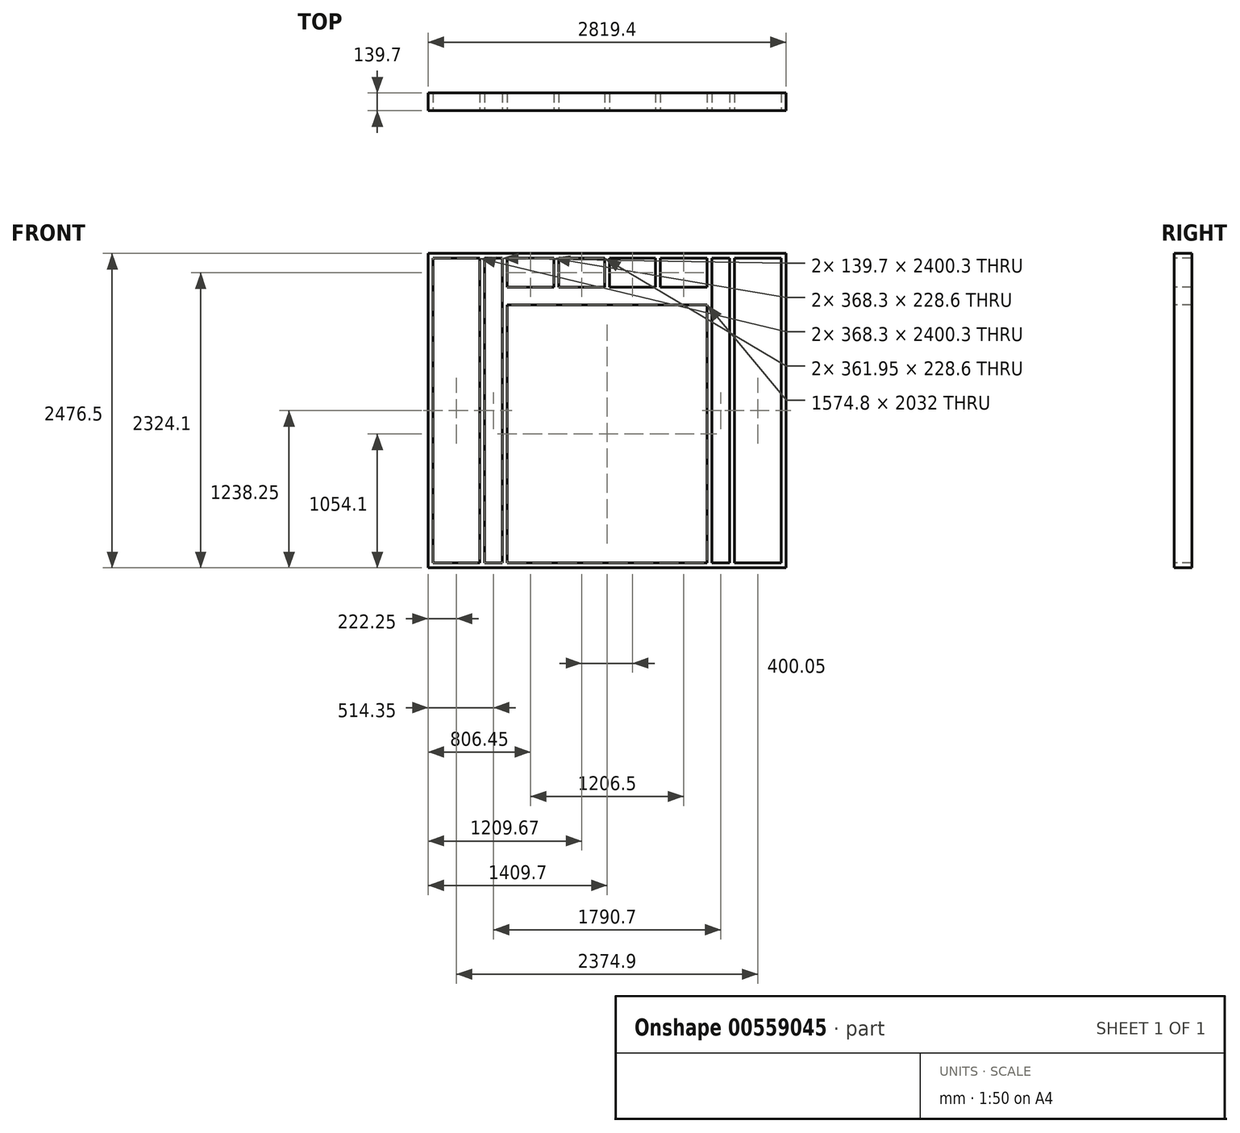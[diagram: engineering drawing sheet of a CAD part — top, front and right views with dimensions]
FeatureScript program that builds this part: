
annotation { "Feature Type Name" : "Feature", "Feature Type Description" : "" }
export const myFeature = defineFeature(function(context is Context, id is Id, definition is map)
    precondition{}
    {
        {
            var Q0;
            Q0=qCreatedBy(makeId("Front.planeOp"),FACE);
            var sketch = newSketch(context, id + "F0", { "sketchPlane" : qUnion([Q0])});
            skLineSegment(sketch, "E0.bottom", {"start": v(0, 0) * mm, "end": v(2819.4, 0) * mm});
            skLineSegment(sketch, "E0.top", {"start": v(0, 2476.5) * mm, "end": v(2819.4, 2476.5) * mm});
            skLineSegment(sketch, "E0.left", {"start": v(0, 0) * mm, "end": v(0, 2476.5) * mm});
            skLineSegment(sketch, "E0.right", {"start": v(2819.4, 0) * mm, "end": v(2819.4, 2476.5) * mm});
            skSolve(sketch);
        }
        {
            var Q0;
            Q0=qSketchRegion(id+"F0",true);
            extrude(context, id + "F1", {"entities" : qUnion([Q0]), "depth" : 139.7 * mm, "offsetDistance" : 25.4 * mm});
        }
        {
            var Q0;
            Q0=makeQuery(id+"F1.opExtrude","CAP_FACE",FACE,{"disambiguationData":[OSD([sQuery(id+"F0.wireOp",EDGE,"E0.bottom"),sQuery(id+"F0.wireOp",EDGE,"E0.top"),sQuery(id+"F0.wireOp",EDGE,"E0.left"),sQuery(id+"F0.wireOp",EDGE,"E0.right")])],"isStart":false});
            var sketch = newSketch(context, id + "F2", { "sketchPlane" : qUnion([Q0])});
            skLineSegment(sketch, "E1.bottom", {"start": v(622.3, 38.1) * mm, "end": v(2197.1, 38.1) * mm});
            skLineSegment(sketch, "E1.top", {"start": v(622.3, 2070.1) * mm, "end": v(2197.1, 2070.1) * mm});
            skLineSegment(sketch, "E1.left", {"start": v(622.3, 38.1) * mm, "end": v(622.3, 2070.1) * mm});
            skLineSegment(sketch, "E1.right", {"start": v(2197.1, 38.1) * mm, "end": v(2197.1, 2070.1) * mm});
            skLineSegment(sketch, "E2", {"start": v(622.3, 38.1) * mm, "end": v(0, 38.1) * mm, "construction": true});
            skLineSegment(sketch, "E3", {"start": v(2197.1, 38.1) * mm, "end": v(2819.4, 38.1) * mm, "construction": true});
            skSolve(sketch);
        }
        {
            var Q0;
            Q0=qSketchRegion(id+"F2",true);
            extrude(context, id + "F3", {"entities" : qUnion([Q0]), "operationType" : NewBodyOperationType.REMOVE, "endBound" : BoundingType.THROUGH_ALL, "oppositeDirection" : true, "depth" : 25.4 * mm, "offsetDistance" : 25.4 * mm});
        }
        {
            var Q0;
            Q0=makeQuery(id+"F1.opExtrude","CAP_FACE",FACE,{"disambiguationData":[OSD([sQuery(id+"F0.wireOp",EDGE,"E0.bottom"),sQuery(id+"F0.wireOp",EDGE,"E0.top"),sQuery(id+"F0.wireOp",EDGE,"E0.left"),sQuery(id+"F0.wireOp",EDGE,"E0.right")])],"isStart":false});
            var sketch = newSketch(context, id + "F4", { "sketchPlane" : qUnion([Q0])});
            skLineSegment(sketch, "E4.bottom", {"start": v(2413, 38.1) * mm, "end": v(2781.3, 38.1) * mm});
            skLineSegment(sketch, "E4.top", {"start": v(2413, 2438.4) * mm, "end": v(2781.3, 2438.4) * mm});
            skLineSegment(sketch, "E4.left", {"start": v(2413, 38.1) * mm, "end": v(2413, 2438.4) * mm});
            skLineSegment(sketch, "E4.right", {"start": v(2781.3, 38.1) * mm, "end": v(2781.3, 2438.4) * mm});
            skLineSegment(sketch, "E5.bottom", {"start": v(2235.2, 38.1) * mm, "end": v(2374.9, 38.1) * mm});
            skLineSegment(sketch, "E5.top", {"start": v(2235.2, 2438.4) * mm, "end": v(2374.9, 2438.4) * mm});
            skLineSegment(sketch, "E5.left", {"start": v(2235.2, 38.1) * mm, "end": v(2235.2, 2438.4) * mm});
            skLineSegment(sketch, "E5.right", {"start": v(2374.9, 38.1) * mm, "end": v(2374.9, 2438.4) * mm});
            skLineSegment(sketch, "E6.bottom", {"start": v(2197.1, 2438.4) * mm, "end": v(1828.8, 2438.4) * mm});
            skLineSegment(sketch, "E6.top", {"start": v(2197.1, 2209.8) * mm, "end": v(1828.8, 2209.8) * mm});
            skLineSegment(sketch, "E6.left", {"start": v(2197.1, 2438.4) * mm, "end": v(2197.1, 2209.8) * mm});
            skLineSegment(sketch, "E6.right", {"start": v(1828.8, 2438.4) * mm, "end": v(1828.8, 2209.8) * mm});
            skLineSegment(sketch, "E7.bottom", {"start": v(38.1, 2438.4) * mm, "end": v(406.4, 2438.4) * mm});
            skLineSegment(sketch, "E7.top", {"start": v(38.1, 38.1) * mm, "end": v(406.4, 38.1) * mm});
            skLineSegment(sketch, "E7.left", {"start": v(38.1, 2438.4) * mm, "end": v(38.1, 38.1) * mm});
            skLineSegment(sketch, "E7.right", {"start": v(406.4, 2438.4) * mm, "end": v(406.4, 38.1) * mm});
            skLineSegment(sketch, "E8.bottom", {"start": v(444.5, 38.1) * mm, "end": v(584.2, 38.1) * mm});
            skLineSegment(sketch, "E8.top", {"start": v(444.5, 2438.4) * mm, "end": v(584.2, 2438.4) * mm});
            skLineSegment(sketch, "E8.left", {"start": v(444.5, 38.1) * mm, "end": v(444.5, 2438.4) * mm});
            skLineSegment(sketch, "E8.right", {"start": v(584.2, 38.1) * mm, "end": v(584.2, 2438.4) * mm});
            skLineSegment(sketch, "E9.bottom", {"start": v(622.3, 2438.4) * mm, "end": v(990.6, 2438.4) * mm});
            skLineSegment(sketch, "E9.top", {"start": v(622.3, 2209.8) * mm, "end": v(990.6, 2209.8) * mm});
            skLineSegment(sketch, "E9.left", {"start": v(622.3, 2438.4) * mm, "end": v(622.3, 2209.8) * mm});
            skLineSegment(sketch, "E9.right", {"start": v(990.6, 2438.4) * mm, "end": v(990.6, 2209.8) * mm});
            skLineSegment(sketch, "E10.bottom", {"start": v(1028.7, 2209.8) * mm, "end": v(1390.65, 2209.8) * mm});
            skLineSegment(sketch, "E10.top", {"start": v(1028.7, 2438.4) * mm, "end": v(1390.65, 2438.4) * mm});
            skLineSegment(sketch, "E10.left", {"start": v(1028.7, 2209.8) * mm, "end": v(1028.7, 2438.4) * mm});
            skLineSegment(sketch, "E10.right", {"start": v(1390.65, 2209.8) * mm, "end": v(1390.65, 2438.4) * mm});
            skLineSegment(sketch, "E11.bottom", {"start": v(1428.75, 2209.8) * mm, "end": v(1790.7, 2209.8) * mm});
            skLineSegment(sketch, "E11.top", {"start": v(1428.75, 2438.4) * mm, "end": v(1790.7, 2438.4) * mm});
            skLineSegment(sketch, "E11.left", {"start": v(1428.75, 2209.8) * mm, "end": v(1428.75, 2438.4) * mm});
            skLineSegment(sketch, "E11.right", {"start": v(1790.7, 2209.8) * mm, "end": v(1790.7, 2438.4) * mm});
            skSolve(sketch);
        }
        {
            var Q0;
            Q0=qSketchRegion(id+"F4",true);
            extrude(context, id + "F5", {"entities" : qUnion([Q0]), "operationType" : NewBodyOperationType.REMOVE, "endBound" : BoundingType.THROUGH_ALL, "oppositeDirection" : true, "depth" : 25.4 * mm, "offsetDistance" : 25.4 * mm});
        }
    });
